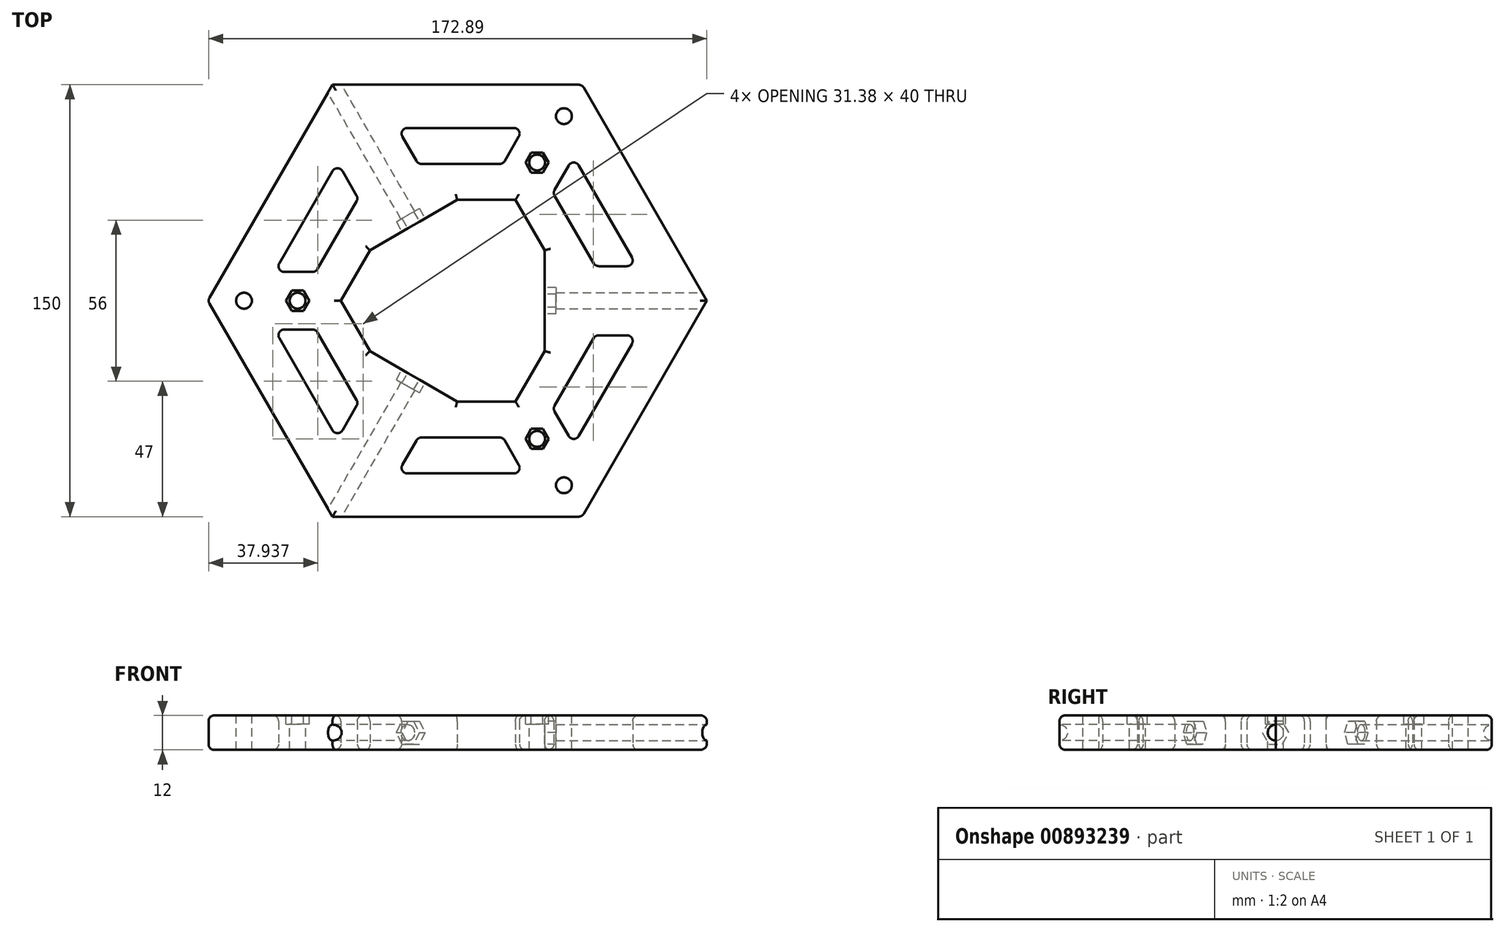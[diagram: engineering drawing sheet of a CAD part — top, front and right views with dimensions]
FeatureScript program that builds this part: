
annotation { "Feature Type Name" : "Feature", "Feature Type Description" : "" }
export const myFeature = defineFeature(function(context is Context, id is Id, definition is map)
    precondition{}
    {
        {
            var Q0;
            Q0=qCreatedBy(makeId("Top.planeOp"),FACE);
            var sketch = newSketch(context, id + "F0", { "sketchPlane" : qUnion([Q0])});
            skLineSegment(sketch, "E0.0", {"start": v(-43.3, 75) * mm, "end": v(43.3, 75) * mm});
            skLineSegment(sketch, "E0.1", {"start": v(43.3, 75) * mm, "end": v(86.6, 0) * mm});
            skLineSegment(sketch, "E0.2", {"start": v(86.6, 0) * mm, "end": v(43.3, -75) * mm});
            skLineSegment(sketch, "E0.3", {"start": v(43.3, -75) * mm, "end": v(-43.3, -75) * mm});
            skLineSegment(sketch, "E0.4", {"start": v(-43.3, -75) * mm, "end": v(-86.6, 0) * mm});
            skLineSegment(sketch, "E0.5", {"start": v(-86.6, 0) * mm, "end": v(-43.3, 75) * mm});
            skLineSegment(sketch, "E1.0", {"start": v(0, 35) * mm, "end": v(20.2, 35) * mm});
            skLineSegment(sketch, "E1.1", {"start": v(20.2, 35) * mm, "end": v(30.31, 17.5) * mm});
            skLineSegment(sketch, "E1.2", {"start": v(30.31, -17.5) * mm, "end": v(20.2, -35) * mm});
            skLineSegment(sketch, "E1.3", {"start": v(20.2, -35) * mm, "end": v(0, -35) * mm});
            skLineSegment(sketch, "E1.4", {"start": v(-30.31, -17.5) * mm, "end": v(-40.41, 0) * mm});
            skLineSegment(sketch, "E1.5", {"start": v(-40.41, 0) * mm, "end": v(-30.31, 17.5) * mm});
            skLineSegment(sketch, "E2", {"start": v(-30.31, 17.5) * mm, "end": v(0, 35) * mm});
            skLineSegment(sketch, "E3", {"start": v(30.31, 17.5) * mm, "end": v(30.31, -17.5) * mm});
            skLineSegment(sketch, "E4", {"start": v(0, -35) * mm, "end": v(-30.31, -17.5) * mm});
            skLineSegment(sketch, "E5.0", {"start": v(-17.32, 60) * mm, "end": v(19.63, 60) * mm});
            skLineSegment(sketch, "E5.1", {"start": v(42.15, 47) * mm, "end": v(60.62, 15) * mm});
            skLineSegment(sketch, "E5.2", {"start": v(60.62, -15) * mm, "end": v(42.15, -47) * mm});
            skLineSegment(sketch, "E5.3", {"start": v(19.63, -60) * mm, "end": v(-17.32, -60) * mm});
            skLineSegment(sketch, "E5.4", {"start": v(-43.3, -45) * mm, "end": v(-61.78, -13) * mm});
            skLineSegment(sketch, "E5.5", {"start": v(-61.78, 13) * mm, "end": v(-43.3, 45) * mm});
            skLineSegment(sketch, "E6.0", {"start": v(-12.41, 47.5) * mm, "end": v(14.72, 47.5) * mm});
            skLineSegment(sketch, "E6.1", {"start": v(33.77, 36.5) * mm, "end": v(47.34, 13) * mm});
            skLineSegment(sketch, "E6.2", {"start": v(47.34, -13) * mm, "end": v(33.77, -36.5) * mm});
            skLineSegment(sketch, "E6.3", {"start": v(14.72, -47.5) * mm, "end": v(-12.41, -47.5) * mm});
            skLineSegment(sketch, "E6.4", {"start": v(-34.93, -34.5) * mm, "end": v(-48.5, -11) * mm});
            skLineSegment(sketch, "E6.5", {"start": v(-48.5, 11) * mm, "end": v(-34.93, 34.5) * mm});
            skLineSegment(sketch, "E7.0", {"start": v(21.36, 57) * mm, "end": v(16.45, 48.5) * mm});
            skLineSegment(sketch, "E8.0", {"start": v(38.68, 47) * mm, "end": v(33.77, 38.5) * mm});
            skLineSegment(sketch, "E9.0", {"start": v(-14.15, 48.5) * mm, "end": v(-19.05, 57) * mm});
            skLineSegment(sketch, "E10.0", {"start": v(-34.93, 36.5) * mm, "end": v(-39.84, 45) * mm});
            skLineSegment(sketch, "E11.0", {"start": v(-50.23, 10) * mm, "end": v(-60.04, 10) * mm});
            skLineSegment(sketch, "E12.0", {"start": v(-50.23, -10) * mm, "end": v(-60.04, -10) * mm});
            skLineSegment(sketch, "E13.0", {"start": v(-14.15, -48.5) * mm, "end": v(-19.05, -57) * mm});
            skLineSegment(sketch, "E14.0", {"start": v(-34.93, -36.5) * mm, "end": v(-39.84, -45) * mm});
            skLineSegment(sketch, "E15.0", {"start": v(33.77, -38.5) * mm, "end": v(38.68, -47) * mm});
            skLineSegment(sketch, "E16.0", {"start": v(16.45, -48.5) * mm, "end": v(21.36, -57) * mm});
            skLineSegment(sketch, "E17.0", {"start": v(58.89, 12) * mm, "end": v(49.07, 12) * mm});
            skLineSegment(sketch, "E18.0", {"start": v(58.89, -12) * mm, "end": v(49.07, -12) * mm});
            skArc(sketch, "E19.filletArc", {"start": v(60.62, -15) * mm, "mid": v(60.62, -13) * mm, "end": v(58.89, -12) * mm});
            skArc(sketch, "E20.filletArc", {"start": v(58.89, 12) * mm, "mid": v(60.62, 13) * mm, "end": v(60.62, 15) * mm});
            skArc(sketch, "E21.filletArc", {"start": v(-19.05, -57) * mm, "mid": v(-19.05, -59) * mm, "end": v(-17.32, -60) * mm});
            skArc(sketch, "E22.filletArc", {"start": v(-43.3, -45) * mm, "mid": v(-41.57, -46) * mm, "end": v(-39.84, -45) * mm});
            skArc(sketch, "E23.filletArc", {"start": v(19.63, -60) * mm, "mid": v(21.36, -59) * mm, "end": v(21.36, -57) * mm});
            skArc(sketch, "E24.filletArc", {"start": v(38.68, -47) * mm, "mid": v(40.41, -48) * mm, "end": v(42.15, -47) * mm});
            skArc(sketch, "E25.filletArc", {"start": v(-61.78, 13) * mm, "mid": v(-61.78, 11) * mm, "end": v(-60.04, 10) * mm});
            skArc(sketch, "E26.filletArc", {"start": v(-60.04, -10) * mm, "mid": v(-61.78, -11) * mm, "end": v(-61.78, -13) * mm});
            skArc(sketch, "E27.filletArc", {"start": v(-17.32, 60) * mm, "mid": v(-19.05, 59) * mm, "end": v(-19.05, 57) * mm});
            skArc(sketch, "E28.filletArc", {"start": v(-39.84, 45) * mm, "mid": v(-41.57, 46) * mm, "end": v(-43.3, 45) * mm});
            skArc(sketch, "E29.filletArc", {"start": v(21.36, 57) * mm, "mid": v(21.36, 59) * mm, "end": v(19.63, 60) * mm});
            skArc(sketch, "E30.filletArc", {"start": v(42.15, 47) * mm, "mid": v(40.41, 48) * mm, "end": v(38.68, 47) * mm});
            skArc(sketch, "E31.filletArc", {"start": v(33.77, -36.5) * mm, "mid": v(33.5, -37.5) * mm, "end": v(33.77, -38.5) * mm});
            skArc(sketch, "E32.filletArc", {"start": v(16.45, -48.5) * mm, "mid": v(15.72, -47.77) * mm, "end": v(14.72, -47.5) * mm});
            skArc(sketch, "E33.filletArc", {"start": v(-12.41, -47.5) * mm, "mid": v(-13.41, -47.77) * mm, "end": v(-14.15, -48.5) * mm});
            skArc(sketch, "E34.filletArc", {"start": v(-34.93, -36.5) * mm, "mid": v(-34.66, -35.5) * mm, "end": v(-34.93, -34.5) * mm});
            skArc(sketch, "E35.filletArc", {"start": v(49.07, -12) * mm, "mid": v(48.07, -12.27) * mm, "end": v(47.34, -13) * mm});
            skArc(sketch, "E36.filletArc", {"start": v(47.34, 13) * mm, "mid": v(48.07, 12.27) * mm, "end": v(49.07, 12) * mm});
            skArc(sketch, "E37.filletArc", {"start": v(14.72, 47.5) * mm, "mid": v(15.72, 47.77) * mm, "end": v(16.45, 48.5) * mm});
            skArc(sketch, "E38.filletArc", {"start": v(33.77, 38.5) * mm, "mid": v(33.5, 37.5) * mm, "end": v(33.77, 36.5) * mm});
            skArc(sketch, "E39.filletArc", {"start": v(-14.15, 48.5) * mm, "mid": v(-13.41, 47.77) * mm, "end": v(-12.41, 47.5) * mm});
            skArc(sketch, "E40.filletArc", {"start": v(-34.93, 34.5) * mm, "mid": v(-34.66, 35.5) * mm, "end": v(-34.93, 36.5) * mm});
            skArc(sketch, "E41.filletArc", {"start": v(-50.23, 10) * mm, "mid": v(-49.23, 10.27) * mm, "end": v(-48.5, 11) * mm});
            skArc(sketch, "E42.filletArc", {"start": v(-48.5, -11) * mm, "mid": v(-49.23, -10.27) * mm, "end": v(-50.23, -10) * mm});
            skPoint(sketch, "E43", {"position": v(37.01, 64.1) * mm});
            skPoint(sketch, "E44", {"position": v(37.01, -64.1) * mm});
            skPoint(sketch, "E45", {"position": v(-74.03, 0) * mm});
            skPoint(sketch, "E46", {"position": v(0, 0) * mm});
            skLineSegment(sketch, "E47", {"start": v(37.01, 64.1) * mm, "end": v(20.2, 35) * mm});
            skLineSegment(sketch, "E48", {"start": v(-74.03, 0) * mm, "end": v(-40.41, 0) * mm});
            skLineSegment(sketch, "E49", {"start": v(37.01, -64.1) * mm, "end": v(20.2, -35) * mm});
            skPoint(sketch, "E50", {"position": v(27.7, -48) * mm});
            skPoint(sketch, "E51", {"position": v(-55.41, 0) * mm});
            skPoint(sketch, "E52", {"position": v(27.7, 48) * mm});
            skLineSegment(sketch, "E53", {"start": v(20.2, -35) * mm, "end": v(0, 0) * mm});
            skLineSegment(sketch, "E54", {"start": v(20.2, 35) * mm, "end": v(0, 0) * mm});
            skLineSegment(sketch, "E55", {"start": v(-40.41, 0) * mm, "end": v(0, 0) * mm});
            skSolve(sketch);
        }
        {
            var Q0;
            Q0=makeQuery(id+"F0.imprint","IMPRINT",FACE,{"disambiguationData":[TD([[makeQuery(id+"F0.imprint","IMPRINT",EDGE,{"derivedFrom":sQuery(id+"F0.wireOp",EDGE,"E0.0")}),-1.0]])]});
            extrude(context, id + "F1", {"entities" : qUnion([Q0]), "depth" : 12 * mm, "offsetDistance" : 25 * mm});
        }
        {
            var Q0;
            Q0=sQuery(id+"F0.wireOp",VERTEX,"E43");
            var Q1;
            Q1=sQuery(id+"F0.wireOp",VERTEX,"E45");
            var Q2;
            Q2=sQuery(id+"F0.wireOp",VERTEX,"E44");
            var Q3;
            Q3=makeQuery(id+"F1.opExtrude","SWEPT_BODY",BODY,{"disambiguationData":[OSD([sQuery(id+"F0.wireOp",EDGE,"E0.0"),sQuery(id+"F0.wireOp",EDGE,"E0.1"),sQuery(id+"F0.wireOp",EDGE,"E0.2"),sQuery(id+"F0.wireOp",EDGE,"E0.3"),sQuery(id+"F0.wireOp",EDGE,"E0.4"),sQuery(id+"F0.wireOp",EDGE,"E0.5"),sQuery(id+"F0.wireOp",EDGE,"E1.0"),sQuery(id+"F0.wireOp",EDGE,"E1.1"),sQuery(id+"F0.wireOp",EDGE,"E1.2"),sQuery(id+"F0.wireOp",EDGE,"E1.3"),sQuery(id+"F0.wireOp",EDGE,"E1.4"),sQuery(id+"F0.wireOp",EDGE,"E1.5"),sQuery(id+"F0.wireOp",EDGE,"E2"),sQuery(id+"F0.wireOp",EDGE,"E3"),sQuery(id+"F0.wireOp",EDGE,"E4"),sQuery(id+"F0.wireOp",EDGE,"E5.0"),sQuery(id+"F0.wireOp",EDGE,"E5.1"),sQuery(id+"F0.wireOp",EDGE,"E5.2"),sQuery(id+"F0.wireOp",EDGE,"E5.3"),sQuery(id+"F0.wireOp",EDGE,"E5.4"),sQuery(id+"F0.wireOp",EDGE,"E5.5"),sQuery(id+"F0.wireOp",EDGE,"E6.0"),sQuery(id+"F0.wireOp",EDGE,"E6.1"),sQuery(id+"F0.wireOp",EDGE,"E6.2"),sQuery(id+"F0.wireOp",EDGE,"E6.3"),sQuery(id+"F0.wireOp",EDGE,"E6.4"),sQuery(id+"F0.wireOp",EDGE,"E6.5"),sQuery(id+"F0.wireOp",EDGE,"E7.0"),sQuery(id+"F0.wireOp",EDGE,"E8.0"),sQuery(id+"F0.wireOp",EDGE,"E9.0"),sQuery(id+"F0.wireOp",EDGE,"E10.0"),sQuery(id+"F0.wireOp",EDGE,"E11.0"),sQuery(id+"F0.wireOp",EDGE,"E12.0"),sQuery(id+"F0.wireOp",EDGE,"E13.0"),sQuery(id+"F0.wireOp",EDGE,"E14.0"),sQuery(id+"F0.wireOp",EDGE,"E15.0"),sQuery(id+"F0.wireOp",EDGE,"E16.0"),sQuery(id+"F0.wireOp",EDGE,"E17.0"),sQuery(id+"F0.wireOp",EDGE,"E18.0"),sQuery(id+"F0.wireOp",EDGE,"E19.filletArc"),sQuery(id+"F0.wireOp",EDGE,"E20.filletArc"),sQuery(id+"F0.wireOp",EDGE,"E21.filletArc"),sQuery(id+"F0.wireOp",EDGE,"E22.filletArc"),sQuery(id+"F0.wireOp",EDGE,"E23.filletArc"),sQuery(id+"F0.wireOp",EDGE,"E24.filletArc"),sQuery(id+"F0.wireOp",EDGE,"E25.filletArc"),sQuery(id+"F0.wireOp",EDGE,"E26.filletArc"),sQuery(id+"F0.wireOp",EDGE,"E27.filletArc"),sQuery(id+"F0.wireOp",EDGE,"E28.filletArc"),sQuery(id+"F0.wireOp",EDGE,"E29.filletArc"),sQuery(id+"F0.wireOp",EDGE,"E30.filletArc"),sQuery(id+"F0.wireOp",EDGE,"E31.filletArc"),sQuery(id+"F0.wireOp",EDGE,"E32.filletArc"),sQuery(id+"F0.wireOp",EDGE,"E33.filletArc"),sQuery(id+"F0.wireOp",EDGE,"E34.filletArc"),sQuery(id+"F0.wireOp",EDGE,"E35.filletArc"),sQuery(id+"F0.wireOp",EDGE,"E36.filletArc"),sQuery(id+"F0.wireOp",EDGE,"E37.filletArc"),sQuery(id+"F0.wireOp",EDGE,"E38.filletArc"),sQuery(id+"F0.wireOp",EDGE,"E39.filletArc"),sQuery(id+"F0.wireOp",EDGE,"E40.filletArc"),sQuery(id+"F0.wireOp",EDGE,"E41.filletArc"),sQuery(id+"F0.wireOp",EDGE,"E42.filletArc")])]});
            hole(context, id + "F2", {"style" : HoleStyle.SIMPLE, "endStyle" : HoleEndStyle.THROUGH, "oppositeDirection" : true, "standardTappedOrClearance" : lookupTablePath({ "fit" : "Normal", "standard" : "ISO", "size" : "M5", "type" : "Clearance" }), "standardBlindInLast" : lookupTablePath({ "fit" : "Normal", "standard" : "ISO", "size" : "M5", "type" : "Clearance" }), "holeDiameter" : 5.5 * mm, "majorDiameter" : 5 * mm, "isTappedThrough" : true, "tappedDepth" : 12 * mm, "tapClearance" : 3, "locations" : qUnion([Q0, Q1, Q2]), "scope" : qUnion([Q3]), "startStyle" : HoleStartStyle.SKETCH});
        }
        {
            var Q0;
            Q0=makeQuery(id+"F1.opExtrude","SWEPT_FACE",FACE,{"disambiguationData":[OSD([sQuery(id+"F0.wireOp",EDGE,"E2")])]});
            var sketch = newSketch(context, id + "F3", { "sketchPlane" : qUnion([Q0])});
            skPoint(sketch, "E56", {"position": v(0, 6) * mm});
            skPoint(sketch, "E56.positionSnap0", {"position": v(17.5, 6) * mm});
            skPoint(sketch, "E56.positionSnap1", {"position": v(0, 10) * mm});
            skCircle(sketch, "E57.cCircle", {"center": v(0, 6) * mm, "radius": 4 * mm, "construction": true});
            skLineSegment(sketch, "E57.0", {"start": v(-2.3, 10) * mm, "end": v(2.3, 10) * mm});
            skLineSegment(sketch, "E57.1", {"start": v(2.3, 10) * mm, "end": v(4.62, 6) * mm});
            skLineSegment(sketch, "E57.2", {"start": v(4.62, 6) * mm, "end": v(2.3, 2) * mm});
            skLineSegment(sketch, "E57.3", {"start": v(2.3, 2) * mm, "end": v(-2.3, 2) * mm});
            skLineSegment(sketch, "E57.4", {"start": v(-2.3, 2) * mm, "end": v(-4.62, 6) * mm});
            skLineSegment(sketch, "E57.5", {"start": v(-4.62, 6) * mm, "end": v(-2.3, 10) * mm});
            skSolve(sketch);
        }
        {
            var Q0;
            Q0=makeQuery(id+"F1.opExtrude","SWEPT_FACE",FACE,{"disambiguationData":[OSD([sQuery(id+"F0.wireOp",EDGE,"E4")])]});
            var sketch = newSketch(context, id + "F4", { "sketchPlane" : qUnion([Q0])});
            skPoint(sketch, "E58", {"position": v(0, 6) * mm});
            skPoint(sketch, "E58.positionSnap0", {"position": v(17.5, 6) * mm});
            skCircle(sketch, "E59.cCircle", {"center": v(0, 6) * mm, "radius": 4 * mm, "construction": true});
            skLineSegment(sketch, "E59.0", {"start": v(2.3, 2) * mm, "end": v(-2.3, 2) * mm});
            skLineSegment(sketch, "E59.1", {"start": v(-2.3, 2) * mm, "end": v(-4.62, 6) * mm});
            skLineSegment(sketch, "E59.2", {"start": v(-4.62, 6) * mm, "end": v(-2.3, 10) * mm});
            skLineSegment(sketch, "E59.3", {"start": v(-2.3, 10) * mm, "end": v(2.3, 10) * mm});
            skLineSegment(sketch, "E59.4", {"start": v(2.3, 10) * mm, "end": v(4.62, 6) * mm});
            skLineSegment(sketch, "E59.5", {"start": v(4.62, 6) * mm, "end": v(2.3, 2) * mm});
            skPoint(sketch, "E59.0.midPoint", {"position": v(0, 2) * mm});
            skSolve(sketch);
        }
        {
            var Q0;
            Q0=makeQuery(id+"F1.opExtrude","SWEPT_FACE",FACE,{"disambiguationData":[OSD([sQuery(id+"F0.wireOp",EDGE,"E3")])]});
            var sketch = newSketch(context, id + "F5", { "sketchPlane" : qUnion([Q0])});
            skPoint(sketch, "E60", {"position": v(0, 6) * mm});
            skPoint(sketch, "E60.positionSnap0", {"position": v(-17.5, 6) * mm});
            skCircle(sketch, "E61.cCircle", {"center": v(0, 6) * mm, "radius": 4 * mm, "construction": true});
            skLineSegment(sketch, "E61.0", {"start": v(-2.3, 10) * mm, "end": v(2.3, 10) * mm});
            skLineSegment(sketch, "E61.1", {"start": v(2.3, 10) * mm, "end": v(4.62, 6) * mm});
            skLineSegment(sketch, "E61.2", {"start": v(4.62, 6) * mm, "end": v(2.3, 2) * mm});
            skLineSegment(sketch, "E61.3", {"start": v(2.3, 2) * mm, "end": v(-2.3, 2) * mm});
            skLineSegment(sketch, "E61.4", {"start": v(-2.3, 2) * mm, "end": v(-4.62, 6) * mm});
            skLineSegment(sketch, "E61.5", {"start": v(-4.62, 6) * mm, "end": v(-2.3, 10) * mm});
            skPoint(sketch, "E61.0.midPoint", {"position": v(0, 10) * mm});
            skSolve(sketch);
        }
        {
            var Q0;
            Q0=sQuery(id+"F5.wireOp",VERTEX,"E60");
            var Q1;
            Q1=sQuery(id+"F3.wireOp",VERTEX,"E56");
            var Q2;
            Q2=sQuery(id+"F4.wireOp",VERTEX,"E58");
            var Q3;
            Q3=makeQuery(id+"F1.opExtrude","SWEPT_BODY",BODY,{"disambiguationData":[OSD([sQuery(id+"F0.wireOp",EDGE,"E0.0"),sQuery(id+"F0.wireOp",EDGE,"E0.1"),sQuery(id+"F0.wireOp",EDGE,"E0.2"),sQuery(id+"F0.wireOp",EDGE,"E0.3"),sQuery(id+"F0.wireOp",EDGE,"E0.4"),sQuery(id+"F0.wireOp",EDGE,"E0.5"),sQuery(id+"F0.wireOp",EDGE,"E1.0"),sQuery(id+"F0.wireOp",EDGE,"E1.1"),sQuery(id+"F0.wireOp",EDGE,"E1.2"),sQuery(id+"F0.wireOp",EDGE,"E1.3"),sQuery(id+"F0.wireOp",EDGE,"E1.4"),sQuery(id+"F0.wireOp",EDGE,"E1.5"),sQuery(id+"F0.wireOp",EDGE,"E2"),sQuery(id+"F0.wireOp",EDGE,"E3"),sQuery(id+"F0.wireOp",EDGE,"E4"),sQuery(id+"F0.wireOp",EDGE,"E5.0"),sQuery(id+"F0.wireOp",EDGE,"E5.1"),sQuery(id+"F0.wireOp",EDGE,"E5.2"),sQuery(id+"F0.wireOp",EDGE,"E5.3"),sQuery(id+"F0.wireOp",EDGE,"E5.4"),sQuery(id+"F0.wireOp",EDGE,"E5.5"),sQuery(id+"F0.wireOp",EDGE,"E6.0"),sQuery(id+"F0.wireOp",EDGE,"E6.1"),sQuery(id+"F0.wireOp",EDGE,"E6.2"),sQuery(id+"F0.wireOp",EDGE,"E6.3"),sQuery(id+"F0.wireOp",EDGE,"E6.4"),sQuery(id+"F0.wireOp",EDGE,"E6.5"),sQuery(id+"F0.wireOp",EDGE,"E7.0"),sQuery(id+"F0.wireOp",EDGE,"E8.0"),sQuery(id+"F0.wireOp",EDGE,"E9.0"),sQuery(id+"F0.wireOp",EDGE,"E10.0"),sQuery(id+"F0.wireOp",EDGE,"E11.0"),sQuery(id+"F0.wireOp",EDGE,"E12.0"),sQuery(id+"F0.wireOp",EDGE,"E13.0"),sQuery(id+"F0.wireOp",EDGE,"E14.0"),sQuery(id+"F0.wireOp",EDGE,"E15.0"),sQuery(id+"F0.wireOp",EDGE,"E16.0"),sQuery(id+"F0.wireOp",EDGE,"E17.0"),sQuery(id+"F0.wireOp",EDGE,"E18.0"),sQuery(id+"F0.wireOp",EDGE,"E19.filletArc"),sQuery(id+"F0.wireOp",EDGE,"E20.filletArc"),sQuery(id+"F0.wireOp",EDGE,"E21.filletArc"),sQuery(id+"F0.wireOp",EDGE,"E22.filletArc"),sQuery(id+"F0.wireOp",EDGE,"E23.filletArc"),sQuery(id+"F0.wireOp",EDGE,"E24.filletArc"),sQuery(id+"F0.wireOp",EDGE,"E25.filletArc"),sQuery(id+"F0.wireOp",EDGE,"E26.filletArc"),sQuery(id+"F0.wireOp",EDGE,"E27.filletArc"),sQuery(id+"F0.wireOp",EDGE,"E28.filletArc"),sQuery(id+"F0.wireOp",EDGE,"E29.filletArc"),sQuery(id+"F0.wireOp",EDGE,"E30.filletArc"),sQuery(id+"F0.wireOp",EDGE,"E31.filletArc"),sQuery(id+"F0.wireOp",EDGE,"E32.filletArc"),sQuery(id+"F0.wireOp",EDGE,"E33.filletArc"),sQuery(id+"F0.wireOp",EDGE,"E34.filletArc"),sQuery(id+"F0.wireOp",EDGE,"E35.filletArc"),sQuery(id+"F0.wireOp",EDGE,"E36.filletArc"),sQuery(id+"F0.wireOp",EDGE,"E37.filletArc"),sQuery(id+"F0.wireOp",EDGE,"E38.filletArc"),sQuery(id+"F0.wireOp",EDGE,"E39.filletArc"),sQuery(id+"F0.wireOp",EDGE,"E40.filletArc"),sQuery(id+"F0.wireOp",EDGE,"E41.filletArc"),sQuery(id+"F0.wireOp",EDGE,"E42.filletArc")])]});
            hole(context, id + "F6", {"style" : HoleStyle.SIMPLE, "endStyle" : HoleEndStyle.THROUGH, "standardTappedOrClearance" : lookupTablePath({ "fit" : "Normal", "standard" : "ISO", "size" : "M5", "type" : "Clearance" }), "standardBlindInLast" : lookupTablePath({ "fit" : "Normal", "standard" : "ISO", "size" : "M5", "type" : "Clearance" }), "holeDiameter" : 5.5 * mm, "majorDiameter" : 5 * mm, "isTappedThrough" : true, "tappedDepth" : 12 * mm, "tapClearance" : 3, "locations" : qUnion([Q0, Q1, Q2]), "scope" : qUnion([Q3]), "startStyle" : HoleStartStyle.SKETCH});
        }
        {
            var Q0;
            Q0=sQuery(id+"F0.wireOp",VERTEX,"E51");
            var Q1;
            Q1=sQuery(id+"F0.wireOp",VERTEX,"E50");
            var Q2;
            Q2=sQuery(id+"F0.wireOp",VERTEX,"E52");
            var Q3;
            Q3=makeQuery(id+"F1.opExtrude","SWEPT_BODY",BODY,{"disambiguationData":[OSD([sQuery(id+"F0.wireOp",EDGE,"E0.0"),sQuery(id+"F0.wireOp",EDGE,"E0.1"),sQuery(id+"F0.wireOp",EDGE,"E0.2"),sQuery(id+"F0.wireOp",EDGE,"E0.3"),sQuery(id+"F0.wireOp",EDGE,"E0.4"),sQuery(id+"F0.wireOp",EDGE,"E0.5"),sQuery(id+"F0.wireOp",EDGE,"E1.0"),sQuery(id+"F0.wireOp",EDGE,"E1.1"),sQuery(id+"F0.wireOp",EDGE,"E1.2"),sQuery(id+"F0.wireOp",EDGE,"E1.3"),sQuery(id+"F0.wireOp",EDGE,"E1.4"),sQuery(id+"F0.wireOp",EDGE,"E1.5"),sQuery(id+"F0.wireOp",EDGE,"E2"),sQuery(id+"F0.wireOp",EDGE,"E3"),sQuery(id+"F0.wireOp",EDGE,"E4"),sQuery(id+"F0.wireOp",EDGE,"E5.0"),sQuery(id+"F0.wireOp",EDGE,"E5.1"),sQuery(id+"F0.wireOp",EDGE,"E5.2"),sQuery(id+"F0.wireOp",EDGE,"E5.3"),sQuery(id+"F0.wireOp",EDGE,"E5.4"),sQuery(id+"F0.wireOp",EDGE,"E5.5"),sQuery(id+"F0.wireOp",EDGE,"E6.0"),sQuery(id+"F0.wireOp",EDGE,"E6.1"),sQuery(id+"F0.wireOp",EDGE,"E6.2"),sQuery(id+"F0.wireOp",EDGE,"E6.3"),sQuery(id+"F0.wireOp",EDGE,"E6.4"),sQuery(id+"F0.wireOp",EDGE,"E6.5"),sQuery(id+"F0.wireOp",EDGE,"E7.0"),sQuery(id+"F0.wireOp",EDGE,"E8.0"),sQuery(id+"F0.wireOp",EDGE,"E9.0"),sQuery(id+"F0.wireOp",EDGE,"E10.0"),sQuery(id+"F0.wireOp",EDGE,"E11.0"),sQuery(id+"F0.wireOp",EDGE,"E12.0"),sQuery(id+"F0.wireOp",EDGE,"E13.0"),sQuery(id+"F0.wireOp",EDGE,"E14.0"),sQuery(id+"F0.wireOp",EDGE,"E15.0"),sQuery(id+"F0.wireOp",EDGE,"E16.0"),sQuery(id+"F0.wireOp",EDGE,"E17.0"),sQuery(id+"F0.wireOp",EDGE,"E18.0"),sQuery(id+"F0.wireOp",EDGE,"E19.filletArc"),sQuery(id+"F0.wireOp",EDGE,"E20.filletArc"),sQuery(id+"F0.wireOp",EDGE,"E21.filletArc"),sQuery(id+"F0.wireOp",EDGE,"E22.filletArc"),sQuery(id+"F0.wireOp",EDGE,"E23.filletArc"),sQuery(id+"F0.wireOp",EDGE,"E24.filletArc"),sQuery(id+"F0.wireOp",EDGE,"E25.filletArc"),sQuery(id+"F0.wireOp",EDGE,"E26.filletArc"),sQuery(id+"F0.wireOp",EDGE,"E27.filletArc"),sQuery(id+"F0.wireOp",EDGE,"E28.filletArc"),sQuery(id+"F0.wireOp",EDGE,"E29.filletArc"),sQuery(id+"F0.wireOp",EDGE,"E30.filletArc"),sQuery(id+"F0.wireOp",EDGE,"E31.filletArc"),sQuery(id+"F0.wireOp",EDGE,"E32.filletArc"),sQuery(id+"F0.wireOp",EDGE,"E33.filletArc"),sQuery(id+"F0.wireOp",EDGE,"E34.filletArc"),sQuery(id+"F0.wireOp",EDGE,"E35.filletArc"),sQuery(id+"F0.wireOp",EDGE,"E36.filletArc"),sQuery(id+"F0.wireOp",EDGE,"E37.filletArc"),sQuery(id+"F0.wireOp",EDGE,"E38.filletArc"),sQuery(id+"F0.wireOp",EDGE,"E39.filletArc"),sQuery(id+"F0.wireOp",EDGE,"E40.filletArc"),sQuery(id+"F0.wireOp",EDGE,"E41.filletArc"),sQuery(id+"F0.wireOp",EDGE,"E42.filletArc")])]});
            hole(context, id + "F7", {"style" : HoleStyle.SIMPLE, "endStyle" : HoleEndStyle.THROUGH, "oppositeDirection" : true, "standardTappedOrClearance" : lookupTablePath({ "fit" : "Normal", "standard" : "ISO", "size" : "M5", "type" : "Clearance" }), "standardBlindInLast" : lookupTablePath({ "fit" : "Normal", "standard" : "ISO", "size" : "M5", "type" : "Clearance" }), "holeDiameter" : 5.5 * mm, "majorDiameter" : 5 * mm, "isTappedThrough" : true, "tappedDepth" : 12 * mm, "tapClearance" : 3, "locations" : qUnion([Q0, Q1, Q2]), "scope" : qUnion([Q3]), "startStyle" : HoleStartStyle.SKETCH});
        }
        {
            var Q0;
            Q0=makeQuery(id+"F1.opExtrude","CAP_FACE",FACE,{"disambiguationData":[OSD([sQuery(id+"F0.wireOp",EDGE,"E0.0"),sQuery(id+"F0.wireOp",EDGE,"E0.1"),sQuery(id+"F0.wireOp",EDGE,"E0.2"),sQuery(id+"F0.wireOp",EDGE,"E0.3"),sQuery(id+"F0.wireOp",EDGE,"E0.4"),sQuery(id+"F0.wireOp",EDGE,"E0.5"),sQuery(id+"F0.wireOp",EDGE,"E1.0"),sQuery(id+"F0.wireOp",EDGE,"E1.1"),sQuery(id+"F0.wireOp",EDGE,"E1.2"),sQuery(id+"F0.wireOp",EDGE,"E1.3"),sQuery(id+"F0.wireOp",EDGE,"E1.4"),sQuery(id+"F0.wireOp",EDGE,"E1.5"),sQuery(id+"F0.wireOp",EDGE,"E2"),sQuery(id+"F0.wireOp",EDGE,"E3"),sQuery(id+"F0.wireOp",EDGE,"E4"),sQuery(id+"F0.wireOp",EDGE,"E5.0"),sQuery(id+"F0.wireOp",EDGE,"E5.1"),sQuery(id+"F0.wireOp",EDGE,"E5.2"),sQuery(id+"F0.wireOp",EDGE,"E5.3"),sQuery(id+"F0.wireOp",EDGE,"E5.4"),sQuery(id+"F0.wireOp",EDGE,"E5.5"),sQuery(id+"F0.wireOp",EDGE,"E6.0"),sQuery(id+"F0.wireOp",EDGE,"E6.1"),sQuery(id+"F0.wireOp",EDGE,"E6.2"),sQuery(id+"F0.wireOp",EDGE,"E6.3"),sQuery(id+"F0.wireOp",EDGE,"E6.4"),sQuery(id+"F0.wireOp",EDGE,"E6.5"),sQuery(id+"F0.wireOp",EDGE,"E7.0"),sQuery(id+"F0.wireOp",EDGE,"E8.0"),sQuery(id+"F0.wireOp",EDGE,"E9.0"),sQuery(id+"F0.wireOp",EDGE,"E10.0"),sQuery(id+"F0.wireOp",EDGE,"E11.0"),sQuery(id+"F0.wireOp",EDGE,"E12.0"),sQuery(id+"F0.wireOp",EDGE,"E13.0"),sQuery(id+"F0.wireOp",EDGE,"E14.0"),sQuery(id+"F0.wireOp",EDGE,"E15.0"),sQuery(id+"F0.wireOp",EDGE,"E16.0"),sQuery(id+"F0.wireOp",EDGE,"E17.0"),sQuery(id+"F0.wireOp",EDGE,"E18.0"),sQuery(id+"F0.wireOp",EDGE,"E19.filletArc"),sQuery(id+"F0.wireOp",EDGE,"E20.filletArc"),sQuery(id+"F0.wireOp",EDGE,"E21.filletArc"),sQuery(id+"F0.wireOp",EDGE,"E22.filletArc"),sQuery(id+"F0.wireOp",EDGE,"E23.filletArc"),sQuery(id+"F0.wireOp",EDGE,"E24.filletArc"),sQuery(id+"F0.wireOp",EDGE,"E25.filletArc"),sQuery(id+"F0.wireOp",EDGE,"E26.filletArc"),sQuery(id+"F0.wireOp",EDGE,"E27.filletArc"),sQuery(id+"F0.wireOp",EDGE,"E28.filletArc"),sQuery(id+"F0.wireOp",EDGE,"E29.filletArc"),sQuery(id+"F0.wireOp",EDGE,"E30.filletArc"),sQuery(id+"F0.wireOp",EDGE,"E31.filletArc"),sQuery(id+"F0.wireOp",EDGE,"E32.filletArc"),sQuery(id+"F0.wireOp",EDGE,"E33.filletArc"),sQuery(id+"F0.wireOp",EDGE,"E34.filletArc"),sQuery(id+"F0.wireOp",EDGE,"E35.filletArc"),sQuery(id+"F0.wireOp",EDGE,"E36.filletArc"),sQuery(id+"F0.wireOp",EDGE,"E37.filletArc"),sQuery(id+"F0.wireOp",EDGE,"E38.filletArc"),sQuery(id+"F0.wireOp",EDGE,"E39.filletArc"),sQuery(id+"F0.wireOp",EDGE,"E40.filletArc"),sQuery(id+"F0.wireOp",EDGE,"E41.filletArc"),sQuery(id+"F0.wireOp",EDGE,"E42.filletArc")])],"isStart":false});
            var sketch = newSketch(context, id + "F8", { "sketchPlane" : qUnion([Q0])});
            skPoint(sketch, "E62", {"position": v(-55.41, 0) * mm});
            skPoint(sketch, "E63", {"position": v(27.7, -48) * mm});
            skPoint(sketch, "E64", {"position": v(27.7, 48) * mm});
            skCircle(sketch, "E65.cCircle", {"center": v(27.7, -48) * mm, "radius": 3.5 * mm, "construction": true});
            skLineSegment(sketch, "E65.0", {"start": v(25.69, -44.5) * mm, "end": v(29.73, -44.5) * mm});
            skLineSegment(sketch, "E65.1", {"start": v(29.73, -44.5) * mm, "end": v(31.75, -48) * mm});
            skLineSegment(sketch, "E65.2", {"start": v(31.75, -48) * mm, "end": v(29.73, -51.5) * mm});
            skLineSegment(sketch, "E65.3", {"start": v(29.73, -51.5) * mm, "end": v(25.69, -51.5) * mm});
            skLineSegment(sketch, "E65.4", {"start": v(25.69, -51.5) * mm, "end": v(23.67, -48) * mm});
            skLineSegment(sketch, "E65.5", {"start": v(23.67, -48) * mm, "end": v(25.69, -44.5) * mm});
            skPoint(sketch, "E65.0.midPoint", {"position": v(27.7, -44.5) * mm});
            skCircle(sketch, "E66.cCircle", {"center": v(27.7, 48) * mm, "radius": 3.5 * mm, "construction": true});
            skLineSegment(sketch, "E66.0", {"start": v(25.69, 51.5) * mm, "end": v(29.73, 51.5) * mm});
            skLineSegment(sketch, "E66.1", {"start": v(29.73, 51.5) * mm, "end": v(31.75, 48) * mm});
            skLineSegment(sketch, "E66.2", {"start": v(31.75, 48) * mm, "end": v(29.73, 44.5) * mm});
            skLineSegment(sketch, "E66.3", {"start": v(29.73, 44.5) * mm, "end": v(25.69, 44.5) * mm});
            skLineSegment(sketch, "E66.4", {"start": v(25.69, 44.5) * mm, "end": v(23.67, 48) * mm});
            skLineSegment(sketch, "E66.5", {"start": v(23.67, 48) * mm, "end": v(25.69, 51.5) * mm});
            skPoint(sketch, "E66.0.midPoint", {"position": v(27.7, 51.5) * mm});
            skCircle(sketch, "E67.cCircle", {"center": v(-55.41, 0) * mm, "radius": 3.5 * mm, "construction": true});
            skLineSegment(sketch, "E67.0", {"start": v(-57.44, 3.5) * mm, "end": v(-53.4, 3.5) * mm});
            skLineSegment(sketch, "E67.1", {"start": v(-53.4, 3.5) * mm, "end": v(-51.37, 0) * mm});
            skLineSegment(sketch, "E67.2", {"start": v(-51.37, 0) * mm, "end": v(-53.4, -3.5) * mm});
            skLineSegment(sketch, "E67.3", {"start": v(-53.4, -3.5) * mm, "end": v(-57.44, -3.5) * mm});
            skLineSegment(sketch, "E67.4", {"start": v(-57.44, -3.5) * mm, "end": v(-59.46, 0) * mm});
            skLineSegment(sketch, "E67.5", {"start": v(-59.46, 0) * mm, "end": v(-57.44, 3.5) * mm});
            skPoint(sketch, "E67.0.midPoint", {"position": v(-55.41, 3.5) * mm});
            skSolve(sketch);
        }
        {
            var Q0;
            Q0=makeQuery(id+"F8.imprint","IMPRINT",FACE,{"disambiguationData":[TD([[makeQuery(id+"F8.imprint","IMPRINT",EDGE,{"derivedFrom":sQuery(id+"F8.wireOp",EDGE,"E67.0")}),-1.0]])]});
            var Q1;
            Q1=makeQuery(id+"F8.imprint","IMPRINT",FACE,{"disambiguationData":[TD([[makeQuery(id+"F8.imprint","IMPRINT",EDGE,{"derivedFrom":sQuery(id+"F8.wireOp",EDGE,"E65.0")}),-1.0]])]});
            var Q2;
            Q2=makeQuery(id+"F8.imprint","IMPRINT",FACE,{"disambiguationData":[TD([[makeQuery(id+"F8.imprint","IMPRINT",EDGE,{"derivedFrom":sQuery(id+"F8.wireOp",EDGE,"E66.0")}),-1.0]])]});
            extrude(context, id + "F9", {"entities" : qUnion([Q0, Q1, Q2]), "operationType" : NewBodyOperationType.REMOVE, "oppositeDirection" : true, "depth" : 3 * mm, "offsetDistance" : 25 * mm});
        }
        {
            var Q0;
            Q0=makeQuery(id+"F1.opExtrude","CAP_EDGE",EDGE,{"disambiguationData":[OSD([sQuery(id+"F0.wireOp",EDGE,"E4")])],"isStart":false});
            var Q1;
            Q1=makeQuery(id+"F1.opExtrude","CAP_EDGE",EDGE,{"disambiguationData":[OSD([sQuery(id+"F0.wireOp",EDGE,"E2")])],"isStart":false});
            var Q2;
            Q2=makeQuery(id+"F1.opExtrude","CAP_EDGE",EDGE,{"disambiguationData":[OSD([sQuery(id+"F0.wireOp",EDGE,"E1.1")])],"isStart":false});
            var Q3;
            Q3=makeQuery(id+"F1.opExtrude","CAP_EDGE",EDGE,{"disambiguationData":[OSD([sQuery(id+"F0.wireOp",EDGE,"E1.0")])],"isStart":false});
            var Q4;
            Q4=makeQuery(id+"F1.opExtrude","CAP_EDGE",EDGE,{"disambiguationData":[OSD([sQuery(id+"F0.wireOp",EDGE,"E3")])],"isStart":false});
            var Q5;
            Q5=makeQuery(id+"F1.opExtrude","CAP_EDGE",EDGE,{"disambiguationData":[OSD([sQuery(id+"F0.wireOp",EDGE,"E1.2")])],"isStart":false});
            var Q6;
            Q6=makeQuery(id+"F1.opExtrude","CAP_EDGE",EDGE,{"disambiguationData":[OSD([sQuery(id+"F0.wireOp",EDGE,"E1.3")])],"isStart":false});
            var Q7;
            Q7=makeQuery(id+"F1.opExtrude","CAP_EDGE",EDGE,{"disambiguationData":[OSD([sQuery(id+"F0.wireOp",EDGE,"E1.5")])],"isStart":false});
            var Q8;
            Q8=makeQuery(id+"F1.opExtrude","CAP_EDGE",EDGE,{"disambiguationData":[OSD([sQuery(id+"F0.wireOp",EDGE,"E1.4")])],"isStart":false});
            var Q9;
            Q9=makeQuery(id+"F1.opExtrude","CAP_EDGE",EDGE,{"disambiguationData":[OSD([sQuery(id+"F0.wireOp",EDGE,"E6.4")])],"isStart":false});
            var Q10;
            Q10=makeQuery(id+"F1.opExtrude","CAP_EDGE",EDGE,{"disambiguationData":[OSD([sQuery(id+"F0.wireOp",EDGE,"E6.2")])],"isStart":false});
            var Q11;
            Q11=makeQuery(id+"F1.opExtrude","CAP_EDGE",EDGE,{"disambiguationData":[OSD([sQuery(id+"F0.wireOp",EDGE,"E6.1")])],"isStart":false});
            var Q12;
            Q12=makeQuery(id+"F1.opExtrude","CAP_EDGE",EDGE,{"disambiguationData":[OSD([sQuery(id+"F0.wireOp",EDGE,"E6.0")])],"isStart":false});
            var Q13;
            Q13=makeQuery(id+"F1.opExtrude","CAP_EDGE",EDGE,{"disambiguationData":[OSD([sQuery(id+"F0.wireOp",EDGE,"E6.5")])],"isStart":false});
            var Q14;
            Q14=makeQuery(id+"F1.opExtrude","CAP_EDGE",EDGE,{"disambiguationData":[OSD([sQuery(id+"F0.wireOp",EDGE,"E6.3")])],"isStart":false});
            var Q15;
            Q15=makeQuery(id+"F1.opExtrude","CAP_EDGE",EDGE,{"disambiguationData":[OSD([sQuery(id+"F0.wireOp",EDGE,"E0.4")])],"isStart":false});
            var Q16;
            Q16=makeQuery(id+"F1.opExtrude","CAP_EDGE",EDGE,{"disambiguationData":[OSD([sQuery(id+"F0.wireOp",EDGE,"E0.1")])],"isStart":false});
            var Q17;
            Q17=makeQuery(id+"F1.opExtrude","CAP_EDGE",EDGE,{"disambiguationData":[OSD([sQuery(id+"F0.wireOp",EDGE,"E0.0")])],"isStart":false});
            var Q18;
            Q18=makeQuery(id+"F1.opExtrude","CAP_EDGE",EDGE,{"disambiguationData":[OSD([sQuery(id+"F0.wireOp",EDGE,"E0.5")])],"isStart":false});
            var Q19;
            Q19=makeQuery(id+"F1.opExtrude","CAP_EDGE",EDGE,{"disambiguationData":[OSD([sQuery(id+"F0.wireOp",EDGE,"E0.2")])],"isStart":false});
            var Q20;
            Q20=makeQuery(id+"F1.opExtrude","CAP_EDGE",EDGE,{"disambiguationData":[OSD([sQuery(id+"F0.wireOp",EDGE,"E0.3")])],"isStart":false});
            var Q21;
            Q21=makeQuery(id+"F1.opExtrude","CAP_EDGE",EDGE,{"disambiguationData":[OSD([sQuery(id+"F0.wireOp",EDGE,"E6.2")])],"isStart":true});
            var Q22;
            Q22=makeQuery(id+"F1.opExtrude","CAP_EDGE",EDGE,{"disambiguationData":[OSD([sQuery(id+"F0.wireOp",EDGE,"E5.1")])],"isStart":true});
            var Q23;
            Q23=makeQuery(id+"F1.opExtrude","CAP_EDGE",EDGE,{"disambiguationData":[OSD([sQuery(id+"F0.wireOp",EDGE,"E5.0")])],"isStart":true});
            var Q24;
            Q24=makeQuery(id+"F1.opExtrude","CAP_EDGE",EDGE,{"disambiguationData":[OSD([sQuery(id+"F0.wireOp",EDGE,"E5.5")])],"isStart":true});
            var Q25;
            Q25=makeQuery(id+"F1.opExtrude","CAP_EDGE",EDGE,{"disambiguationData":[OSD([sQuery(id+"F0.wireOp",EDGE,"E6.4")])],"isStart":true});
            var Q26;
            Q26=makeQuery(id+"F1.opExtrude","CAP_EDGE",EDGE,{"disambiguationData":[OSD([sQuery(id+"F0.wireOp",EDGE,"E5.3")])],"isStart":true});
            var Q27;
            Q27=makeQuery(id+"F1.opExtrude","CAP_EDGE",EDGE,{"disambiguationData":[OSD([sQuery(id+"F0.wireOp",EDGE,"E2")])],"isStart":true});
            var Q28;
            Q28=makeQuery(id+"F1.opExtrude","CAP_EDGE",EDGE,{"disambiguationData":[OSD([sQuery(id+"F0.wireOp",EDGE,"E1.5")])],"isStart":true});
            var Q29;
            Q29=makeQuery(id+"F1.opExtrude","CAP_EDGE",EDGE,{"disambiguationData":[OSD([sQuery(id+"F0.wireOp",EDGE,"E1.0")])],"isStart":true});
            var Q30;
            Q30=makeQuery(id+"F1.opExtrude","CAP_EDGE",EDGE,{"disambiguationData":[OSD([sQuery(id+"F0.wireOp",EDGE,"E3")])],"isStart":true});
            var Q31;
            Q31=makeQuery(id+"F1.opExtrude","CAP_EDGE",EDGE,{"disambiguationData":[OSD([sQuery(id+"F0.wireOp",EDGE,"E1.2")])],"isStart":true});
            var Q32;
            Q32=makeQuery(id+"F1.opExtrude","CAP_EDGE",EDGE,{"disambiguationData":[OSD([sQuery(id+"F0.wireOp",EDGE,"E1.4")])],"isStart":true});
            var Q33;
            Q33=makeQuery(id+"F1.opExtrude","CAP_EDGE",EDGE,{"disambiguationData":[OSD([sQuery(id+"F0.wireOp",EDGE,"E1.3")])],"isStart":true});
            var Q34;
            Q34=makeQuery(id+"F1.opExtrude","CAP_EDGE",EDGE,{"disambiguationData":[OSD([sQuery(id+"F0.wireOp",EDGE,"E0.1")])],"isStart":true});
            var Q35;
            Q35=makeQuery(id+"F1.opExtrude","CAP_EDGE",EDGE,{"disambiguationData":[OSD([sQuery(id+"F0.wireOp",EDGE,"E0.2")])],"isStart":true});
            var Q36;
            Q36=makeQuery(id+"F1.opExtrude","CAP_EDGE",EDGE,{"disambiguationData":[OSD([sQuery(id+"F0.wireOp",EDGE,"E0.3")])],"isStart":true});
            var Q37;
            Q37=makeQuery(id+"F1.opExtrude","CAP_EDGE",EDGE,{"disambiguationData":[OSD([sQuery(id+"F0.wireOp",EDGE,"E0.4")])],"isStart":true});
            var Q38;
            Q38=makeQuery(id+"F1.opExtrude","CAP_EDGE",EDGE,{"disambiguationData":[OSD([sQuery(id+"F0.wireOp",EDGE,"E0.0")])],"isStart":true});
            var Q39;
            Q39=makeQuery(id+"F1.opExtrude","CAP_EDGE",EDGE,{"disambiguationData":[OSD([sQuery(id+"F0.wireOp",EDGE,"E4")])],"isStart":true});
            var Q40;
            Q40=makeQuery(id+"F1.opExtrude","CAP_EDGE",EDGE,{"disambiguationData":[OSD([sQuery(id+"F0.wireOp",EDGE,"E1.1")])],"isStart":true});
            var Q41;
            Q41=makeQuery(id+"F1.opExtrude","CAP_EDGE",EDGE,{"disambiguationData":[OSD([sQuery(id+"F0.wireOp",EDGE,"E0.5")])],"isStart":true});
            var Q42;
            Q42=makeQuery(id+"F1.opExtrude","SWEPT_EDGE",EDGE,{"disambiguationData":[OSD([sQuery(id+"F0.wireOp",EDGE,"E0.4"),sQuery(id+"F0.wireOp",EDGE,"E0.5")])]});
            var Q43;
            Q43=makeQuery(id+"F1.opExtrude","SWEPT_EDGE",EDGE,{"disambiguationData":[OSD([sQuery(id+"F0.wireOp",EDGE,"E0.2"),sQuery(id+"F0.wireOp",EDGE,"E0.3")])]});
            var Q44;
            Q44=makeQuery(id+"F1.opExtrude","SWEPT_EDGE",EDGE,{"disambiguationData":[OSD([sQuery(id+"F0.wireOp",EDGE,"E0.0"),sQuery(id+"F0.wireOp",EDGE,"E0.1")])]});
            fillet(context, id + "F10", {"entities" : qUnion([Q0, Q1, Q2, Q3, Q4, Q5, Q6, Q7, Q8, Q9, Q10, Q11, Q12, Q13, Q14, Q15, Q16, Q17, Q18, Q19, Q20, Q21, Q22, Q23, Q24, Q25, Q26, Q27, Q28, Q29, Q30, Q31, Q32, Q33, Q34, Q35, Q36, Q37, Q38, Q39, Q40, Q41, Q42, Q43, Q44]), "radius" : 2 * mm, "tangentPropagation" : true, "allowEdgeOverflow" : false});
        }
        {
            var Q0;
            Q0=makeQuery(id+"F3.imprint","IMPRINT",FACE,{"disambiguationData":[TD([[makeQuery(id+"F3.imprint","IMPRINT",EDGE,{"derivedFrom":sQuery(id+"F3.wireOp",EDGE,"E57.0")}),-1.0]])]});
            extrude(context, id + "F11", {"entities" : qUnion([Q0]), "operationType" : NewBodyOperationType.REMOVE, "oppositeDirection" : true, "depth" : 4 * mm, "offsetDistance" : 25 * mm});
        }
        {
            var Q0;
            Q0=makeQuery(id+"F4.imprint","IMPRINT",FACE,{"disambiguationData":[TD([[makeQuery(id+"F4.imprint","IMPRINT",EDGE,{"derivedFrom":sQuery(id+"F4.wireOp",EDGE,"E59.0")}),-1.0]])]});
            extrude(context, id + "F12", {"entities" : qUnion([Q0]), "operationType" : NewBodyOperationType.REMOVE, "oppositeDirection" : true, "depth" : 4 * mm, "offsetDistance" : 25 * mm});
        }
        {
            var Q0;
            Q0=makeQuery(id+"F5.imprint","IMPRINT",FACE,{"disambiguationData":[TD([[makeQuery(id+"F5.imprint","IMPRINT",EDGE,{"derivedFrom":sQuery(id+"F5.wireOp",EDGE,"E61.0")}),-1.0]])]});
            extrude(context, id + "F13", {"entities" : qUnion([Q0]), "operationType" : NewBodyOperationType.REMOVE, "oppositeDirection" : true, "depth" : 4 * mm, "offsetDistance" : 25 * mm});
        }
    });
